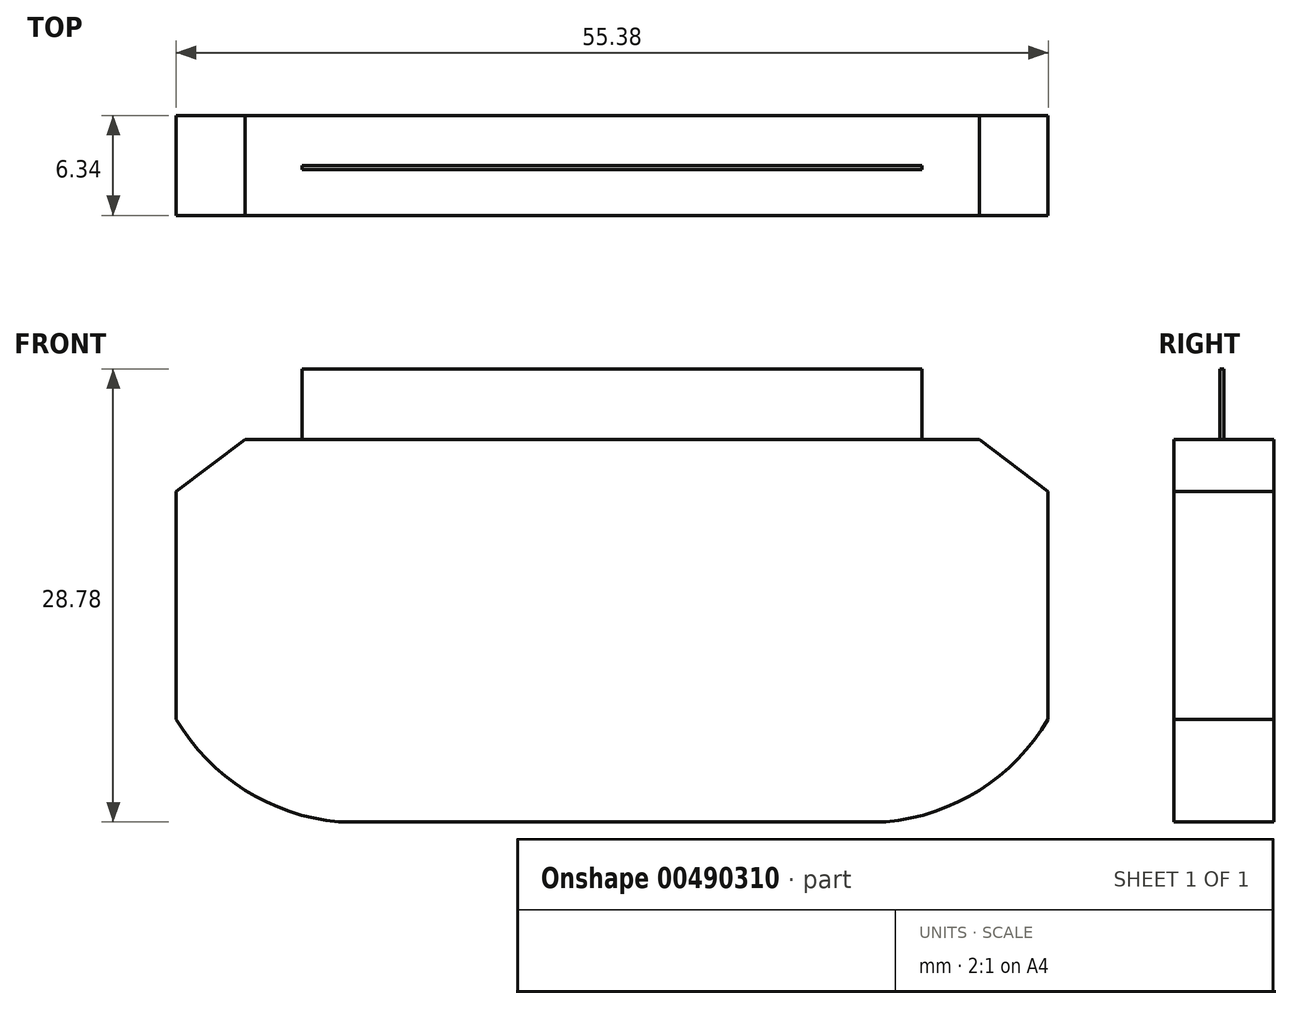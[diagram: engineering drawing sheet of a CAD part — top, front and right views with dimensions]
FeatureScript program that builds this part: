
annotation { "Feature Type Name" : "Feature", "Feature Type Description" : "" }
export const myFeature = defineFeature(function(context is Context, id is Id, definition is map)
    precondition{}
    {
        {
            var Q0;
            Q0=qCreatedBy(makeId("Front.planeOp"),FACE);
            var sketch = newSketch(context, id + "F0", { "sketchPlane" : qUnion([Q0])});
            skLineSegment(sketch, "E0.bottom", {"start": v(19.69, -9.52) * mm, "end": v(-19.69, -9.53) * mm});
            skLineSegment(sketch, "E0.top", {"start": v(19.69, 9.53) * mm, "end": v(-19.69, 9.52) * mm});
            skLineSegment(sketch, "E0.left", {"start": v(19.69, -9.52) * mm, "end": v(19.69, 9.53) * mm});
            skLineSegment(sketch, "E0.right", {"start": v(-19.69, -9.53) * mm, "end": v(-19.69, 9.52) * mm});
            skPoint(sketch, "E0.middle", {"position": v(0, 0) * mm});
            skLineSegment(sketch, "E1.left", {"start": v(1.57, -1.06) * mm, "end": v(1.57, 3) * mm});
            skLineSegment(sketch, "E1.right", {"start": v(-1.47, -1.06) * mm, "end": v(-1.47, 3) * mm});
            skPoint(sketch, "E1.middle", {"position": v(0.05, 0.97) * mm});
            skPoint(sketch, "E2.visualSharp", {"position": v(1.57, 4.52) * mm});
            skArc(sketch, "E2.filletArc", {"start": v(1.57, 3) * mm, "mid": v(1.09, 4.12) * mm, "end": v(-0.06, 4.52) * mm});
            skPoint(sketch, "E3.visualSharp", {"position": v(-1.47, 4.52) * mm});
            skArc(sketch, "E3.filletArc", {"start": v(0.05, 4.52) * mm, "mid": v(-1.03, 4.08) * mm, "end": v(-1.47, 3) * mm});
            skPoint(sketch, "E4.visualSharp", {"position": v(-1.47, -2.59) * mm});
            skArc(sketch, "E4.filletArc", {"start": v(-1.47, -1.06) * mm, "mid": v(-1.04, -2.13) * mm, "end": v(0.02, -2.59) * mm});
            skPoint(sketch, "E5.visualSharp", {"position": v(1.57, -2.59) * mm});
            skArc(sketch, "E5.filletArc", {"start": v(0.02, -2.59) * mm, "mid": v(1.12, -2.15) * mm, "end": v(1.57, -1.06) * mm});
            skArc(sketch, "E6", {"start": v(-15.67, -1.52) * mm, "mid": v(-14.07, -0.01) * mm, "end": v(-15.65, 1.52) * mm});
            skArc(sketch, "E7", {"start": v(-19.87, -2.8) * mm, "mid": v(-18.42, -2.5) * mm, "end": v(-17.32, -1.52) * mm});
            skArc(sketch, "E8", {"start": v(-17.32, 1.52) * mm, "mid": v(-18.4, 2.5) * mm, "end": v(-19.8, 2.8) * mm});
            skLineSegment(sketch, "E9", {"start": v(-17.32, 1.52) * mm, "end": v(-15.65, 1.52) * mm});
            skLineSegment(sketch, "E10", {"start": v(-15.67, -1.52) * mm, "end": v(-17.32, -1.52) * mm});
            skArc(sketch, "E11.MirrorCS", {"start": v(19.87, -2.8) * mm, "mid": v(18.42, -2.5) * mm, "end": v(17.32, -1.52) * mm});
            skLineSegment(sketch, "E12.MirrorCS", {"start": v(17.32, 1.52) * mm, "end": v(15.65, 1.52) * mm});
            skLineSegment(sketch, "E13.MirrorCS", {"start": v(15.67, -1.52) * mm, "end": v(17.32, -1.52) * mm});
            skArc(sketch, "E14.MirrorCS", {"start": v(15.67, -1.52) * mm, "mid": v(14.07, -0.01) * mm, "end": v(15.65, 1.52) * mm});
            skArc(sketch, "E15.MirrorCS", {"start": v(17.32, 1.52) * mm, "mid": v(18.4, 2.5) * mm, "end": v(19.8, 2.8) * mm});
            skSolve(sketch);
        }
        {
            var Q0;
            Q0=makeQuery(id+"F0.imprint","IMPRINT",FACE,{"disambiguationData":[TD([[makeQuery(id+"F0.imprint","IMPRINT",EDGE,{"derivedFrom":sQuery(id+"F0.wireOp",EDGE,"E0.bottom")}),-1.0]])]});
            extrude(context, id + "F1", {"entities" : qUnion([Q0]), "depth" : 0.25 * mm});
        }
        {
            var Q0;
            Q0=makeQuery(id+"F1.opExtrude","CAP_FACE",FACE,{"disambiguationData":[OSD([sQuery(id+"F0.wireOp",EDGE,"E0.bottom"),sQuery(id+"F0.wireOp",EDGE,"E0.top"),sQuery(id+"F0.wireOp",EDGE,"E0.left"),sQuery(id+"F0.wireOp",EDGE,"E0.right")])],"isStart":false});
            var sketch = newSketch(context, id + "F2", { "sketchPlane" : qUnion([Q0])});
            skLineSegment(sketch, "E16.bottom", {"start": v(-19.69, -9.53) * mm, "end": v(19.69, -9.53) * mm});
            skLineSegment(sketch, "E16.top", {"start": v(-19.69, -2.41) * mm, "end": v(19.69, -2.41) * mm});
            skLineSegment(sketch, "E16.left", {"start": v(-19.69, -9.53) * mm, "end": v(-19.69, -2.41) * mm});
            skLineSegment(sketch, "E16.right", {"start": v(19.69, -9.53) * mm, "end": v(19.69, -2.41) * mm});
            skSolve(sketch);
        }
        {
            var Q0;
            Q0=makeQuery(id+"F2.imprint","IMPRINT",FACE,{"disambiguationData":[TD([[makeQuery(id+"F2.imprint","IMPRINT",EDGE,{"derivedFrom":sQuery(id+"F2.wireOp",EDGE,"E16.bottom")}),-1.0]])]});
            extrude(context, id + "F3", {"entities" : qUnion([Q0]), "operationType" : NewBodyOperationType.ADD, "depth" : 0.5 * mm});
        }
        {
            var Q0;
            Q0=makeQuery(id+"F3.opExtrude","CAP_FACE",FACE,{"disambiguationData":[OSD([sQuery(id+"F2.wireOp",EDGE,"E16.bottom"),sQuery(id+"F2.wireOp",EDGE,"E16.top"),sQuery(id+"F2.wireOp",EDGE,"E16.left"),sQuery(id+"F2.wireOp",EDGE,"E16.right")])],"isStart":false});
            extrude(context, id + "F4", {"entities" : qUnion([Q0]), "operationType" : NewBodyOperationType.ADD, "depth" : -1.27 * mm});
        }
        {
            var Q0;
            Q0=qCreatedBy(makeId("Front.planeOp"),FACE);
            var sketch = newSketch(context, id + "F5", { "sketchPlane" : qUnion([Q0])});
            skLineSegment(sketch, "E17", {"start": v(-23.31, 5.05) * mm, "end": v(-27.69, 1.75) * mm});
            skLineSegment(sketch, "E18", {"start": v(-27.69, 1.75) * mm, "end": v(-27.69, -12.73) * mm});
            skArc(sketch, "E19", {"start": v(-27.69, -12.73) * mm, "mid": v(-23.32, -17.23) * mm, "end": v(-17.38, -19.25) * mm});
            skArc(sketch, "E20.MirrorCS", {"start": v(27.69, -12.73) * mm, "mid": v(23.32, -17.23) * mm, "end": v(17.38, -19.25) * mm});
            skLineSegment(sketch, "E21.MirrorCS", {"start": v(23.31, 5.05) * mm, "end": v(27.69, 1.75) * mm});
            skLineSegment(sketch, "E22.MirrorCS", {"start": v(27.69, 1.75) * mm, "end": v(27.69, -12.73) * mm});
            skLineSegment(sketch, "E23", {"start": v(-17.38, -19.25) * mm, "end": v(17.38, -19.25) * mm});
            skLineSegment(sketch, "E24", {"start": v(23.31, 5.05) * mm, "end": v(-23.31, 5.05) * mm});
            skSolve(sketch);
        }
        {
            var Q0;
            Q0=makeQuery(id+"F1.opExtrude","SWEPT_BODY",BODY,{"disambiguationData":[OSD([sQuery(id+"F0.wireOp",EDGE,"E0.bottom"),sQuery(id+"F0.wireOp",EDGE,"E0.top"),sQuery(id+"F0.wireOp",EDGE,"E0.left"),sQuery(id+"F0.wireOp",EDGE,"E0.right"),sQuery(id+"F0.wireOp",EDGE,"E1.left"),sQuery(id+"F0.wireOp",EDGE,"E1.right"),sQuery(id+"F0.wireOp",EDGE,"E2.filletArc"),sQuery(id+"F0.wireOp",EDGE,"E3.filletArc"),sQuery(id+"F0.wireOp",EDGE,"E4.filletArc"),sQuery(id+"F0.wireOp",EDGE,"E5.filletArc"),sQuery(id+"F0.wireOp",EDGE,"E6"),sQuery(id+"F0.wireOp",EDGE,"E7"),sQuery(id+"F0.wireOp",EDGE,"E8"),sQuery(id+"F0.wireOp",EDGE,"E9"),sQuery(id+"F0.wireOp",EDGE,"E10"),sQuery(id+"F0.wireOp",EDGE,"E11.MirrorCS"),sQuery(id+"F0.wireOp",EDGE,"E12.MirrorCS"),sQuery(id+"F0.wireOp",EDGE,"E13.MirrorCS"),sQuery(id+"F0.wireOp",EDGE,"E14.MirrorCS"),sQuery(id+"F0.wireOp",EDGE,"E15.MirrorCS")])]});
            transform(context, id + "F6", {"entities" : qUnion([Q0]), "transformType" : TransformType.TRANSLATION_3D, "dx" : 0 * mm, "dy" : 0 * mm, "dz" : 0 * mm, "makeCopy" : true});
        }
        {
            var Q0;
            Q0=qCreatedBy(makeId("Right.planeOp"),FACE);
            cPlane(context, id + "F7", {"entities" : qUnion([Q0]), "cplaneType" : CPlaneType.OFFSET, "offset" : 25.4 * mm, "width" : 152.4 * mm, "height" : 152.4 * mm});
        }
        {
            var Q0;
            Q0 = qSketchRegion(id + "F5", true);
            extrude(context, id + "F8", {"entities" : qUnion([Q0]), "operationType" : NewBodyOperationType.ADD, "endBound" : BoundingType.SYMMETRIC, "depth" : 6.35 * mm});
        }
    });
